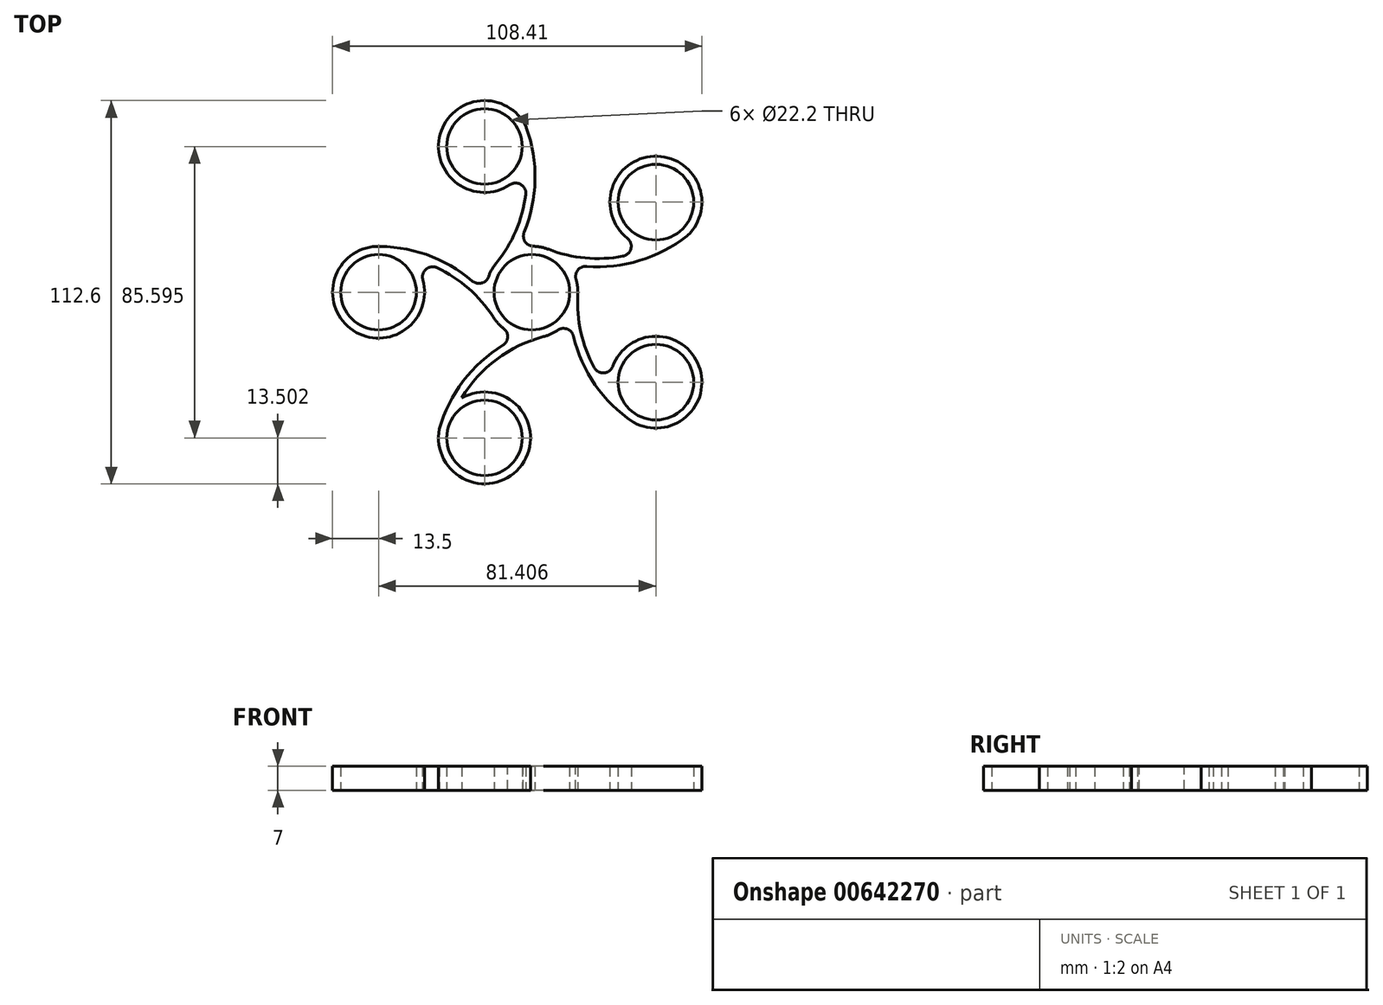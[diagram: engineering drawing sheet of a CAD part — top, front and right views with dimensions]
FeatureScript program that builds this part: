
annotation { "Feature Type Name" : "Feature", "Feature Type Description" : "" }
export const myFeature = defineFeature(function(context is Context, id is Id, definition is map)
    precondition{}
    {
        {
            var Q0;
            Q0=qCreatedBy(makeId("Top.planeOp"),FACE);
            var sketch = newSketch(context, id + "F0", { "sketchPlane" : qUnion([Q0])});
            skCircle(sketch, "E0", {"center": v(0, 0) * mm, "radius": 11.1 * mm});
            skArc(sketch, "E1", {"start": v(-10.46, 8.53) * mm, "mid": v(7.86, -10.97) * mm, "end": v(-4.72, 12.65) * mm});
            skLineSegment(sketch, "E2", {"start": v(0, 0) * mm, "end": v(-45, 0) * mm, "construction": true});
            skCircle(sketch, "E3", {"center": v(-45, 0) * mm, "radius": 11.1 * mm});
            skCircle(sketch, "E4", {"center": v(-45, 0) * mm, "radius": 13.5 * mm});
            skLineSegment(sketch, "E5", {"start": v(-45, 0) * mm, "end": v(-45, -13.5) * mm, "construction": true});
            skLineSegment(sketch, "E6", {"start": v(0, 0) * mm, "end": v(0, 13.5) * mm, "construction": true});
            skLineSegment(sketch, "E7", {"start": v(-45, 0) * mm, "end": v(-35.45, -9.55) * mm, "construction": true});
            skLineSegment(sketch, "E8", {"start": v(0, 0) * mm, "end": v(-9.55, 9.55) * mm});
            skLineSegment(sketch, "E9", {"start": v(0, 0) * mm, "end": v(0, -13.5) * mm, "construction": true});
            skLineSegment(sketch, "E10", {"start": v(0, 0) * mm, "end": v(-9.55, -9.55) * mm, "construction": true});
            skCircle(sketch, "E11.1.1", {"center": v(-13.9, -42.8) * mm, "radius": 13.5 * mm});
            skLineSegment(sketch, "E11.1.3", {"start": v(-13.9, -42.8) * mm, "end": v(-1.07, -46.97) * mm, "construction": true});
            skCircle(sketch, "E11.1.4", {"center": v(-13.9, -42.8) * mm, "radius": 11.1 * mm});
            skLineSegment(sketch, "E11.1.5", {"start": v(-13.9, -42.8) * mm, "end": v(-1.88, -36.67) * mm, "construction": true});
            skCircle(sketch, "E11.2.1", {"center": v(36.4, -26.45) * mm, "radius": 13.5 * mm});
            skLineSegment(sketch, "E11.2.3", {"start": v(36.4, -26.45) * mm, "end": v(44.34, -15.53) * mm, "construction": true});
            skCircle(sketch, "E11.2.4", {"center": v(36.4, -26.45) * mm, "radius": 11.1 * mm});
            skLineSegment(sketch, "E11.2.5", {"start": v(36.4, -26.45) * mm, "end": v(34.3, -13.12) * mm, "construction": true});
            skCircle(sketch, "E11.3.1", {"center": v(36.4, 26.45) * mm, "radius": 13.5 * mm});
            skLineSegment(sketch, "E11.3.3", {"start": v(36.4, 26.45) * mm, "end": v(28.47, 37.37) * mm, "construction": true});
            skCircle(sketch, "E11.3.4", {"center": v(36.4, 26.45) * mm, "radius": 11.1 * mm});
            skLineSegment(sketch, "E11.3.5", {"start": v(36.4, 26.45) * mm, "end": v(23.07, 28.56) * mm, "construction": true});
            skCircle(sketch, "E11.4.1", {"center": v(-13.9, 42.8) * mm, "radius": 13.5 * mm});
            skLineSegment(sketch, "E11.4.3", {"start": v(-13.9, 42.8) * mm, "end": v(-26.75, 38.63) * mm, "construction": true});
            skCircle(sketch, "E11.4.4", {"center": v(-13.9, 42.8) * mm, "radius": 11.1 * mm});
            skLineSegment(sketch, "E11.4.5", {"start": v(-13.9, 42.8) * mm, "end": v(-20.03, 30.77) * mm, "construction": true});
            skLineSegment(sketch, "E12", {"start": v(-45, 0) * mm, "end": v(-45, -29) * mm, "construction": true});
            skArc(sketch, "E13", {"start": v(-46.6, 13.4) * mm, "mid": v(-64.6, -66.63) * mm, "end": v(-9.33, -6.01) * mm, "construction": true});
            skArc(sketch, "E14", {"start": v(-13.49, -0.58) * mm, "mid": v(-28.49, 10.1) * mm, "end": v(-46.6, 13.4) * mm});
            skArc(sketch, "E15", {"start": v(-11.35, -7.31) * mm, "mid": v(-21.95, 3.73) * mm, "end": v(-35.92, 10) * mm});
            skArc(sketch, "E16", {"start": v(-43.6, 11.01) * mm, "mid": v(-64.78, -63.8) * mm, "end": v(-11.35, -7.31) * mm, "construction": true});
            skArc(sketch, "E17.1.0", {"start": v(3.45, -13.05) * mm, "mid": v(-10.33, -19.72) * mm, "end": v(-20.6, -31.08) * mm});
            skArc(sketch, "E17.2.0", {"start": v(13.48, -0.75) * mm, "mid": v(15.56, -15.92) * mm, "end": v(23.19, -29.2) * mm});
            skArc(sketch, "E17.2.1", {"start": v(11.25, -7.46) * mm, "mid": v(17.12, -24.91) * mm, "end": v(29.82, -38.24) * mm});
            skArc(sketch, "E17.3.0", {"start": v(4.88, 12.59) * mm, "mid": v(19.95, 9.88) * mm, "end": v(34.94, 13.03) * mm});
            skArc(sketch, "E17.3.1", {"start": v(10.57, 8.4) * mm, "mid": v(28.98, 8.58) * mm, "end": v(45.58, 16.55) * mm});
            skArc(sketch, "E17.4.0", {"start": v(-10.46, 8.53) * mm, "mid": v(-3.23, 22.03) * mm, "end": v(-1.6, 37.25) * mm});
            skArc(sketch, "E18.trimOffspring", {"start": v(-3.62, -13) * mm, "mid": v(-18.4, -23.98) * mm, "end": v(-27.15, -40.18) * mm});
            skPoint(sketch, "E19.orphan", {"position": v(-23.94, -38.06) * mm});
            skPoint(sketch, "E20.orphan", {"position": v(28.8, -34.53) * mm});
            skPoint(sketch, "E21.orphan", {"position": v(41.74, 16.71) * mm});
            skPoint(sketch, "E22.orphan", {"position": v(-3, 44.86) * mm});
            skPoint(sketch, "E23.orphan", {"position": v(4.01, 10.35) * mm});
            skArc(sketch, "E24.trimOffspring", {"start": v(-4.72, 12.65) * mm, "mid": v(0.8, 30.21) * mm, "end": v(-1.65, 48.46) * mm});
            skPoint(sketch, "E25.orphan", {"position": v(11.08, -0.62) * mm});
            skSolve(sketch);
        }
        {
            var Q0;
            Q0=makeQuery(id+"F0.imprint","IMPRINT",FACE,{"disambiguationData":[TD([[makeQuery(id+"F0.imprint","IMPRINT",EDGE,{"derivedFrom":sQuery(id+"F0.wireOp",EDGE,"E0")}),-1.0]])]});
            var Q1;
            {var subQ0=sQuery(id+"F0.wireOp",EDGE,"e56zxMKM-Kjhy-064L-GIG7-PTHqFccnnUyJ");var subQ1=sQuery(id+"F0.wireOp",EDGE,"E1");var subQ2=makeQuery(id+"F0.imprint","INTERSECT",VERTEX,{"derivedFrom":[subQ1,subQ0]});Q1=makeQuery(id+"F0.imprint","IMPRINT",FACE,{"disambiguationData":[TD([[makeQuery(id+"F0.imprint","IMPRINT",EDGE,{"disambiguationData":[TD([[subQ2,-1.0]])],"derivedFrom":subQ1}),-1.0]])]});}
            var Q2;
            Q2=makeQuery(id+"F0.imprint","IMPRINT",FACE,{"disambiguationData":[TD([[makeQuery(id+"F0.imprint","IMPRINT",EDGE,{"derivedFrom":sQuery(id+"F0.wireOp",EDGE,"0e4e4f05-918f-47c3-9332-bcd5f5d39093.1.4.0")}),-1.0]])]});
            var Q3;
            {var subQ0=sQuery(id+"F0.wireOp",EDGE,"2f779958-1fc4-4bb9-a079-996d55da559e.1.0");var subQ1=sQuery(id+"F0.wireOp",EDGE,"E1");var subQ2=makeQuery(id+"F0.imprint","INTERSECT",VERTEX,{"derivedFrom":[subQ1,subQ0]});Q3=makeQuery(id+"F0.imprint","IMPRINT",FACE,{"disambiguationData":[TD([[makeQuery(id+"F0.imprint","IMPRINT",EDGE,{"disambiguationData":[TD([[subQ2,-1.0]])],"derivedFrom":subQ1}),-1.0]])]});}
            var Q4;
            Q4=makeQuery(id+"F0.imprint","IMPRINT",FACE,{"disambiguationData":[TD([[makeQuery(id+"F0.imprint","IMPRINT",EDGE,{"derivedFrom":sQuery(id+"F0.wireOp",EDGE,"E3")}),-1.0]])]});
            var Q5;
            {var subQ0=sQuery(id+"F0.wireOp",EDGE,"2f779958-1fc4-4bb9-a079-996d55da559e.2.0");var subQ1=sQuery(id+"F0.wireOp",EDGE,"E1");var subQ2=makeQuery(id+"F0.imprint","INTERSECT",VERTEX,{"derivedFrom":[subQ1,subQ0]});Q5=makeQuery(id+"F0.imprint","IMPRINT",FACE,{"disambiguationData":[TD([[makeQuery(id+"F0.imprint","IMPRINT",EDGE,{"disambiguationData":[TD([[subQ2,-1.0]])],"derivedFrom":subQ1}),-1.0]])]});}
            var Q6;
            Q6=makeQuery(id+"F0.imprint","IMPRINT",FACE,{"disambiguationData":[TD([[makeQuery(id+"F0.imprint","IMPRINT",EDGE,{"derivedFrom":sQuery(id+"F0.wireOp",EDGE,"2dce2605-6ec3-4248-8eab-4bc886ecd383.1.0")}),-1.0]])]});
            var Q7;
            {var subQ0=sQuery(id+"F0.wireOp",EDGE,"2f779958-1fc4-4bb9-a079-996d55da559e.3.0");var subQ1=sQuery(id+"F0.wireOp",EDGE,"E1");var subQ2=makeQuery(id+"F0.imprint","INTERSECT",VERTEX,{"derivedFrom":[subQ1,subQ0]});Q7=makeQuery(id+"F0.imprint","IMPRINT",FACE,{"disambiguationData":[TD([[makeQuery(id+"F0.imprint","IMPRINT",EDGE,{"disambiguationData":[TD([[subQ2,-1.0]])],"derivedFrom":subQ1}),-1.0]])]});}
            var Q8;
            Q8=makeQuery(id+"F0.imprint","IMPRINT",FACE,{"disambiguationData":[TD([[makeQuery(id+"F0.imprint","IMPRINT",EDGE,{"derivedFrom":sQuery(id+"F0.wireOp",EDGE,"2dce2605-6ec3-4248-8eab-4bc886ecd383.2.0")}),-1.0]])]});
            var Q9;
            {var subQ0=sQuery(id+"F0.wireOp",EDGE,"2f779958-1fc4-4bb9-a079-996d55da559e.4.0");var subQ1=sQuery(id+"F0.wireOp",EDGE,"E1");var subQ2=makeQuery(id+"F0.imprint","INTERSECT",VERTEX,{"derivedFrom":[subQ1,subQ0]});Q9=makeQuery(id+"F0.imprint","IMPRINT",FACE,{"disambiguationData":[TD([[makeQuery(id+"F0.imprint","IMPRINT",EDGE,{"disambiguationData":[TD([[subQ2,-1.0]])],"derivedFrom":subQ1}),-1.0]])]});}
            var Q10;
            Q10=makeQuery(id+"F0.imprint","IMPRINT",FACE,{"disambiguationData":[TD([[makeQuery(id+"F0.imprint","IMPRINT",EDGE,{"derivedFrom":sQuery(id+"F0.wireOp",EDGE,"0e4e4f05-918f-47c3-9332-bcd5f5d39093.1.3.0")}),-1.0]])]});
            var Q11;
            Q11=makeQuery(id+"F0.imprint","IMPRINT",FACE,{"disambiguationData":[TD([[makeQuery(id+"F0.imprint","IMPRINT",EDGE,{"derivedFrom":sQuery(id+"F0.wireOp",EDGE,"E11.4.4")}),-1.0]])]});
            var Q12;
            Q12=makeQuery(id+"F0.imprint","IMPRINT",FACE,{"disambiguationData":[TD([[makeQuery(id+"F0.imprint","IMPRINT",EDGE,{"derivedFrom":sQuery(id+"F0.wireOp",EDGE,"E11.3.4")}),-1.0]])]});
            var Q13;
            Q13=makeQuery(id+"F0.imprint","IMPRINT",FACE,{"disambiguationData":[TD([[makeQuery(id+"F0.imprint","IMPRINT",EDGE,{"derivedFrom":sQuery(id+"F0.wireOp",EDGE,"E11.2.4")}),-1.0]])]});
            var Q14;
            Q14=makeQuery(id+"F0.imprint","IMPRINT",FACE,{"disambiguationData":[TD([[makeQuery(id+"F0.imprint","IMPRINT",EDGE,{"derivedFrom":sQuery(id+"F0.wireOp",EDGE,"E11.1.4")}),-1.0]])]});
            extrude(context, id + "F1", {"entities" : qUnion([Q0, Q1, Q2, Q3, Q4, Q5, Q6, Q7, Q8, Q9, Q10, Q11, Q12, Q13, Q14]), "depth" : 7 * mm, "offsetDistance" : 25 * mm});
        }
        {
            var Q0;
            Q0=makeQuery(id+"F1.opExtrude","SWEPT_EDGE",EDGE,{"disambiguationData":[OSD([sQuery(id+"F0.wireOp",EDGE,"E4"),sQuery(id+"F0.wireOp",EDGE,"862f28d8-1a82-4196-a4d7-3373fb334ef9.trimOffspring")])]});
            var Q1;
            Q1=makeQuery(id+"F1.opExtrude","SWEPT_EDGE",EDGE,{"disambiguationData":[OSD([sQuery(id+"F0.wireOp",EDGE,"E11.4.0"),sQuery(id+"F0.wireOp",EDGE,"E11.4.1")])]});
            var Q2;
            Q2=makeQuery(id+"F1.opExtrude","SWEPT_EDGE",EDGE,{"disambiguationData":[OSD([sQuery(id+"F0.wireOp",EDGE,"E11.3.0"),sQuery(id+"F0.wireOp",EDGE,"E11.3.1")])]});
            var Q3;
            Q3=makeQuery(id+"F1.opExtrude","SWEPT_EDGE",EDGE,{"disambiguationData":[OSD([sQuery(id+"F0.wireOp",EDGE,"E1"),sQuery(id+"F0.wireOp",EDGE,"E11.1.2")])]});
            var Q4;
            Q4=makeQuery(id+"F1.opExtrude","SWEPT_EDGE",EDGE,{"disambiguationData":[OSD([sQuery(id+"F0.wireOp",EDGE,"E11.2.0"),sQuery(id+"F0.wireOp",EDGE,"E11.2.1")])]});
            var Q5;
            Q5=makeQuery(id+"F1.opExtrude","SWEPT_EDGE",EDGE,{"disambiguationData":[OSD([sQuery(id+"F0.wireOp",EDGE,"E1"),sQuery(id+"F0.wireOp",EDGE,"E11.4.2")])]});
            var Q6;
            Q6=makeQuery(id+"F1.opExtrude","SWEPT_EDGE",EDGE,{"disambiguationData":[OSD([sQuery(id+"F0.wireOp",EDGE,"E1"),sQuery(id+"F0.wireOp",EDGE,"E11.3.2")])]});
            var Q7;
            Q7=makeQuery(id+"F1.opExtrude","SWEPT_EDGE",EDGE,{"disambiguationData":[OSD([sQuery(id+"F0.wireOp",EDGE,"E1"),sQuery(id+"F0.wireOp",EDGE,"E11.2.2")])]});
            var Q8;
            Q8=makeQuery(id+"F1.opExtrude","SWEPT_EDGE",EDGE,{"disambiguationData":[OSD([sQuery(id+"F0.wireOp",EDGE,"E1"),sQuery(id+"F0.wireOp",EDGE,"2f5197a4-56eb-4991-870d-5f60ac515c6a.trimOffspring")])]});
            fillet(context, id + "F2", {"entities" : qUnion([Q0, Q1, Q2, Q3, Q4, Q5, Q6, Q7, Q8]), "radius" : 3 * mm, "tangentPropagation" : true, "allowEdgeOverflow" : false});
        }
    });
